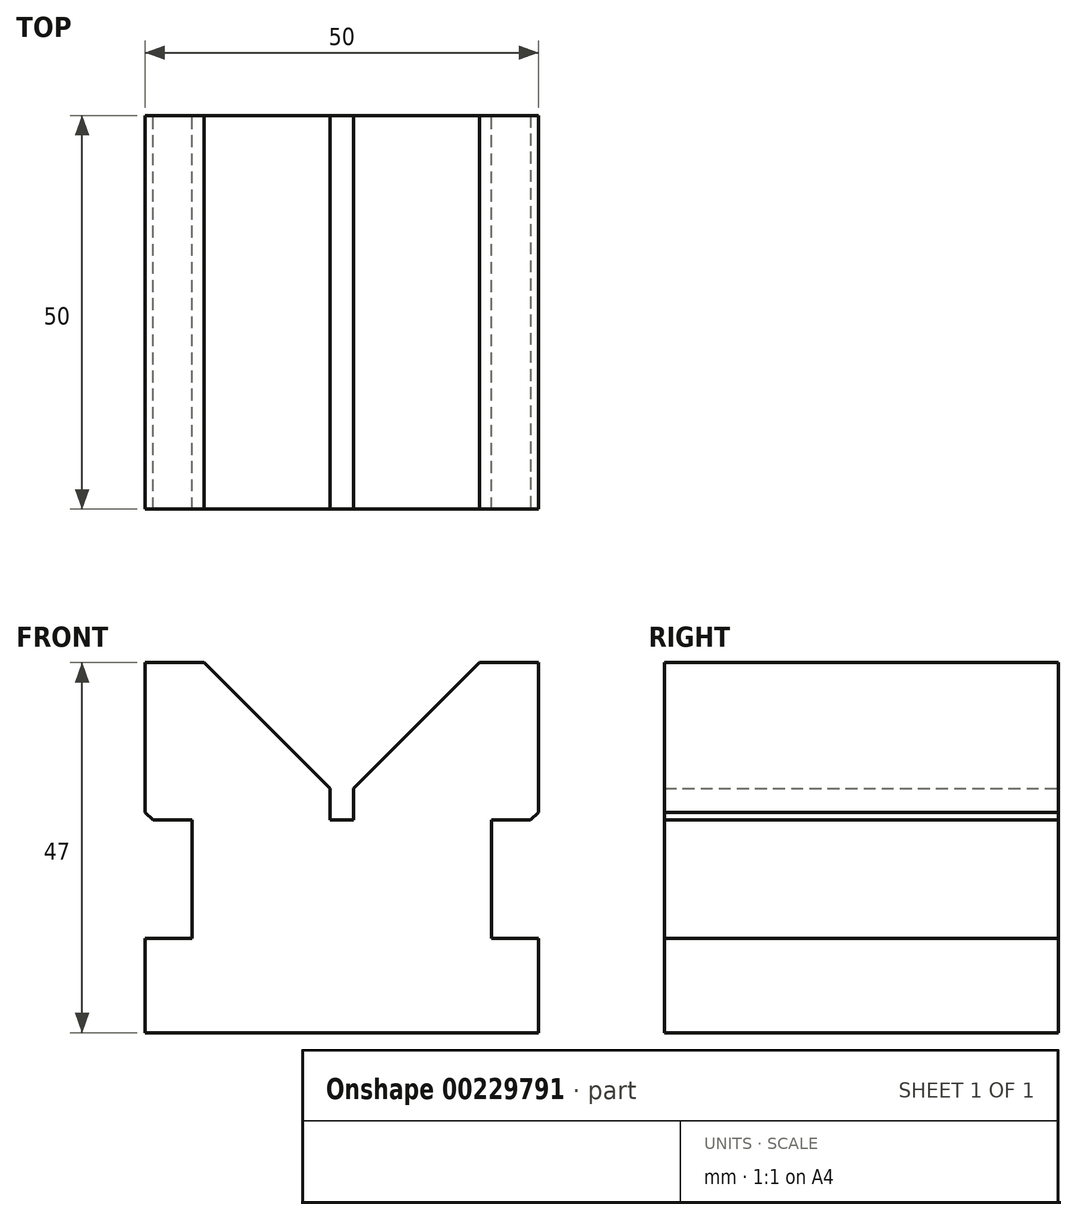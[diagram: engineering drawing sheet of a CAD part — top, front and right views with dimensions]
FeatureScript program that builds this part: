
annotation { "Feature Type Name" : "Feature", "Feature Type Description" : "" }
export const myFeature = defineFeature(function(context is Context, id is Id, definition is map)
    precondition{}
    {
        {
            var Q0;
            Q0=qCreatedBy(makeId("Front.planeOp"),FACE);
            var sketch = newSketch(context, id + "F0", { "sketchPlane" : qUnion([Q0])});
            skLineSegment(sketch, "E0", {"start": v(-25, -27) * mm, "end": v(25, -27) * mm});
            skLineSegment(sketch, "E1", {"start": v(25, -27) * mm, "end": v(25, -15) * mm});
            skLineSegment(sketch, "E2", {"start": v(25, -15) * mm, "end": v(19, -15) * mm});
            skLineSegment(sketch, "E3", {"start": v(19, -15) * mm, "end": v(19, 0) * mm});
            skLineSegment(sketch, "E4", {"start": v(19, 0) * mm, "end": v(25, 0) * mm});
            skLineSegment(sketch, "E5", {"start": v(25, 0) * mm, "end": v(25, 20) * mm});
            skLineSegment(sketch, "E6", {"start": v(25, 20) * mm, "end": v(17.5, 20) * mm});
            skLineSegment(sketch, "E7", {"start": v(17.5, 20) * mm, "end": v(1.5, 4) * mm});
            skLineSegment(sketch, "E8", {"start": v(1.5, 4) * mm, "end": v(1.5, 0) * mm});
            skLineSegment(sketch, "E9", {"start": v(1.5, 0) * mm, "end": v(-1.5, 0) * mm});
            skLineSegment(sketch, "E10", {"start": v(-1.5, 0) * mm, "end": v(-1.5, 4) * mm});
            skLineSegment(sketch, "E11", {"start": v(-1.5, 4) * mm, "end": v(-17.5, 20) * mm});
            skLineSegment(sketch, "E12", {"start": v(-17.5, 20) * mm, "end": v(-25, 20) * mm});
            skLineSegment(sketch, "E13", {"start": v(-25, 20) * mm, "end": v(-25, 0) * mm});
            skLineSegment(sketch, "E14", {"start": v(-25, 0) * mm, "end": v(-19, 0) * mm});
            skLineSegment(sketch, "E15", {"start": v(-19, 0) * mm, "end": v(-19, -15) * mm});
            skLineSegment(sketch, "E16", {"start": v(-19, -15) * mm, "end": v(-25, -15) * mm});
            skLineSegment(sketch, "E17", {"start": v(-25, -15) * mm, "end": v(-25, -27) * mm});
            skSolve(sketch);
        }
        {
            var Q0;
            Q0=makeQuery(id+"F0.imprint","IMPRINT",FACE,{"disambiguationData":[TD([[makeQuery(id+"F0.imprint","IMPRINT",EDGE,{"derivedFrom":sQuery(id+"F0.wireOp",EDGE,"E0")}),1.0]])]});
            extrude(context, id + "F1", {"entities" : qUnion([Q0]), "endBound" : BoundingType.SYMMETRIC, "depth" : 50 * mm});
        }
        {
            var Q0;
            Q0=makeQuery(id+"F1.opExtrude","SWEPT_EDGE",EDGE,{"disambiguationData":[OSD([sQuery(id+"F0.wireOp",EDGE,"E4"),sQuery(id+"F0.wireOp",EDGE,"E5")])]});
            var Q1;
            Q1=makeQuery(id+"F1.opExtrude","SWEPT_EDGE",EDGE,{"disambiguationData":[OSD([sQuery(id+"F0.wireOp",EDGE,"E13"),sQuery(id+"F0.wireOp",EDGE,"E14")])]});
            chamfer(context, id + "F2", {"entities" : qUnion([Q0, Q1]), "chamferType" : ChamferType.OFFSET_ANGLE, "width" : 1 * mm, "oppositeDirection" : false, "angle" : 45 * degree, "tangentPropagation" : true});
        }
    });
